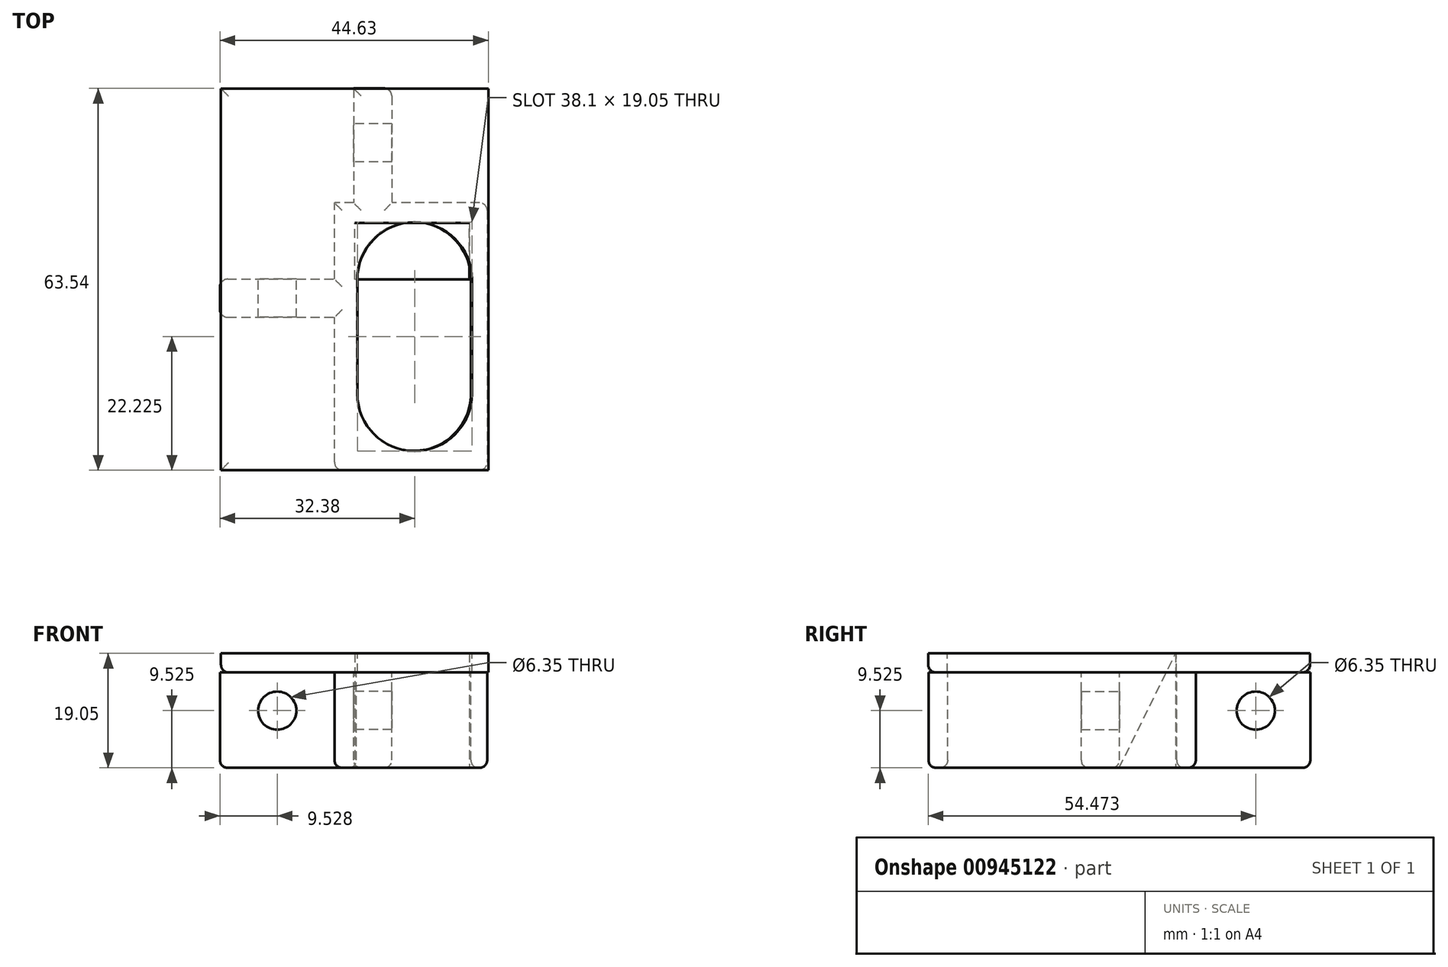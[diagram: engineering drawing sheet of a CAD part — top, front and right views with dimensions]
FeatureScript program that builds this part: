
annotation { "Feature Type Name" : "Feature", "Feature Type Description" : "" }
export const myFeature = defineFeature(function(context is Context, id is Id, definition is map)
    precondition{}
    {
        {
            var Q0;
            Q0=qCreatedBy(makeId("Top.planeOp"),FACE);
            cPlane(context, id + "F0", {"entities" : qUnion([Q0]), "cplaneType" : CPlaneType.OFFSET, "offset" : 3.17 * mm, "oppositeDirection" : true, "width" : 152.4 * mm, "height" : 152.4 * mm});
        }
        {
            var Q0;
            Q0=qCreatedBy(id+"F0.planeOp",FACE);
            var sketch = newSketch(context, id + "F1", { "sketchPlane" : qUnion([Q0])});
            skLineSegment(sketch, "E0.bottom", {"start": v(-22.4, 31.8) * mm, "end": v(22.05, 31.8) * mm});
            skLineSegment(sketch, "E0.top", {"start": v(-22.4, -31.7) * mm, "end": v(22.05, -31.7) * mm});
            skLineSegment(sketch, "E0.left", {"start": v(-22.4, 31.8) * mm, "end": v(-22.4, -31.7) * mm});
            skLineSegment(sketch, "E0.right", {"start": v(22.05, 31.8) * mm, "end": v(22.05, -31.7) * mm});
            skPoint(sketch, "E0.middle", {"position": v(-0.17, 0.04) * mm});
            skLineSegment(sketch, "E1.bottom", {"start": v(22.05, -31.7) * mm, "end": v(-3.35, -31.7) * mm});
            skLineSegment(sketch, "E1.top", {"start": v(22.05, 12.74) * mm, "end": v(-3.35, 12.74) * mm});
            skLineSegment(sketch, "E1.left", {"start": v(22.05, -31.7) * mm, "end": v(22.05, 12.74) * mm});
            skLineSegment(sketch, "E1.right", {"start": v(-3.35, -31.7) * mm, "end": v(-3.35, 12.74) * mm});
            skLineSegment(sketch, "E2", {"start": v(-3.35, 9.57) * mm, "end": v(22.05, 9.57) * mm, "construction": true});
            skLineSegment(sketch, "E3", {"start": v(-3.35, -28.53) * mm, "end": v(22.05, -28.53) * mm, "construction": true});
            skPoint(sketch, "E3.endSnap0", {"position": v(22.05, -9.48) * mm});
            skArc(sketch, "E4", {"start": v(19.33, 0.04) * mm, "mid": v(9.8, 9.57) * mm, "end": v(0.28, 0.04) * mm});
            skLineSegment(sketch, "E5", {"start": v(0.28, 0.04) * mm, "end": v(0.28, -9.48) * mm});
            skLineSegment(sketch, "E6", {"start": v(19.33, 0.04) * mm, "end": v(19.33, -9.48) * mm});
            skLineSegment(sketch, "E7", {"start": v(0.28, -9.48) * mm, "end": v(19.33, -9.48) * mm, "construction": true});
            skLineSegment(sketch, "E8", {"start": v(19.33, -9.48) * mm, "end": v(22.05, -9.48) * mm, "construction": true});
            skArc(sketch, "E9.MirrorCS", {"start": v(19.33, -19) * mm, "mid": v(9.8, -28.53) * mm, "end": v(0.28, -19) * mm});
            skLineSegment(sketch, "E10.MirrorCS", {"start": v(0.28, -19) * mm, "end": v(0.28, -9.48) * mm});
            skLineSegment(sketch, "E11.MirrorCS", {"start": v(19.33, -19) * mm, "end": v(19.33, -9.48) * mm});
            skLineSegment(sketch, "E12", {"start": v(-0.17, 31.8) * mm, "end": v(-0.17, 12.74) * mm});
            skLineSegment(sketch, "E13", {"start": v(6.18, 31.8) * mm, "end": v(6.18, 12.74) * mm});
            skLineSegment(sketch, "E14", {"start": v(-22.4, 0.04) * mm, "end": v(-3.35, 0.04) * mm});
            skLineSegment(sketch, "E15", {"start": v(-22.4, -6.3) * mm, "end": v(-3.35, -6.3) * mm});
            skSolve(sketch);
        }
        {
            var Q0;
            Q0=qCreatedBy(makeId("Top.planeOp"),FACE);
            var sketch = newSketch(context, id + "F2", { "sketchPlane" : qUnion([Q0])});
            skLineSegment(sketch, "E16.bottom", {"start": v(-22.23, 31.75) * mm, "end": v(22.23, 31.75) * mm});
            skLineSegment(sketch, "E16.top", {"start": v(-22.23, -31.75) * mm, "end": v(22.22, -31.75) * mm});
            skLineSegment(sketch, "E16.left", {"start": v(-22.22, 31.75) * mm, "end": v(-22.23, -31.75) * mm});
            skLineSegment(sketch, "E16.right", {"start": v(22.23, 31.75) * mm, "end": v(22.22, -31.75) * mm});
            skPoint(sketch, "E16.middle", {"position": v(0, 0) * mm});
            skLineSegment(sketch, "E17.bottom", {"start": v(22.22, -31.75) * mm, "end": v(-3.18, -31.75) * mm});
            skLineSegment(sketch, "E17.top", {"start": v(22.22, 12.7) * mm, "end": v(-3.18, 12.7) * mm});
            skLineSegment(sketch, "E17.left", {"start": v(22.22, -31.75) * mm, "end": v(22.22, 12.7) * mm});
            skLineSegment(sketch, "E17.right", {"start": v(-3.18, -31.75) * mm, "end": v(-3.18, 12.7) * mm});
            skLineSegment(sketch, "E18", {"start": v(-3.18, 9.53) * mm, "end": v(22.22, 9.53) * mm, "construction": true});
            skLineSegment(sketch, "E19", {"start": v(-3.17, -28.58) * mm, "end": v(22.23, -28.57) * mm, "construction": true});
            skPoint(sketch, "E19.endSnap0", {"position": v(22.23, -9.52) * mm});
            skArc(sketch, "E20", {"start": v(19.5, 0) * mm, "mid": v(9.98, 9.52) * mm, "end": v(0.46, 0) * mm});
            skLineSegment(sketch, "E21", {"start": v(0.46, 0) * mm, "end": v(0.46, -9.53) * mm});
            skLineSegment(sketch, "E22", {"start": v(19.5, 0) * mm, "end": v(19.5, -9.52) * mm});
            skLineSegment(sketch, "E23", {"start": v(0.46, -9.53) * mm, "end": v(19.5, -9.52) * mm, "construction": true});
            skLineSegment(sketch, "E24", {"start": v(19.5, -9.52) * mm, "end": v(22.23, -9.52) * mm, "construction": true});
            skArc(sketch, "E25.MirrorCS", {"start": v(19.5, -19.05) * mm, "mid": v(9.98, -28.57) * mm, "end": v(0.46, -19.05) * mm});
            skLineSegment(sketch, "E26.MirrorCS", {"start": v(0.46, -19.05) * mm, "end": v(0.46, -9.52) * mm});
            skLineSegment(sketch, "E27.MirrorCS", {"start": v(19.5, -19.05) * mm, "end": v(19.5, -9.52) * mm});
            skLineSegment(sketch, "E28", {"start": v(0, 31.75) * mm, "end": v(0, 12.7) * mm});
            skLineSegment(sketch, "E29", {"start": v(6.35, 31.75) * mm, "end": v(6.35, 12.7) * mm});
            skLineSegment(sketch, "E30", {"start": v(-22.23, 0) * mm, "end": v(-3.17, 0) * mm});
            skLineSegment(sketch, "E31", {"start": v(-22.23, -6.35) * mm, "end": v(-3.17, -6.35) * mm});
            skSolve(sketch);
        }
        {
            var Q0;
            {var subQ4=sQuery(id+"F2.wireOp",EDGE,"E28");Q0=makeQuery(id+"F2.imprint","IMPRINT",FACE,{"disambiguationData":[TD([[makeQuery(id+"F2.imprint","IMPRINT",EDGE,{"derivedFrom":subQ4}),-1.0]])]});}
            var Q1;
            {var subQ5=sQuery(id+"F2.wireOp",EDGE,"E31");Q1=makeQuery(id+"F2.imprint","IMPRINT",FACE,{"disambiguationData":[TD([[makeQuery(id+"F2.imprint","IMPRINT",EDGE,{"derivedFrom":subQ5}),-1.0]])]});}
            var Q2;
            {var subQ0=sQuery(id+"F2.wireOp",EDGE,"E29");Q2=makeQuery(id+"F2.imprint","IMPRINT",FACE,{"disambiguationData":[TD([[makeQuery(id+"F2.imprint","IMPRINT",EDGE,{"derivedFrom":subQ0}),1.0]])]});}
            var Q3;
            {var subQ2=sQuery(id+"F2.wireOp",EDGE,"E30");Q3=makeQuery(id+"F2.imprint","IMPRINT",FACE,{"disambiguationData":[TD([[makeQuery(id+"F2.imprint","IMPRINT",EDGE,{"derivedFrom":subQ2}),-1.0]])]});}
            var Q4;
            {var subQ2=sQuery(id+"F2.wireOp",EDGE,"E28");Q4=makeQuery(id+"F2.imprint","IMPRINT",FACE,{"disambiguationData":[TD([[makeQuery(id+"F2.imprint","IMPRINT",EDGE,{"derivedFrom":subQ2}),1.0]])]});}
            var Q5;
            Q5=makeQuery(id+"F2.imprint","IMPRINT",FACE,{"disambiguationData":[TD([[makeQuery(id+"F2.imprint","IMPRINT",EDGE,{"derivedFrom":sQuery(id+"F2.wireOp",EDGE,"E20")}),-1.0]])]});
            extrude(context, id + "F3", {"entities" : qUnion([Q0, Q1, Q2, Q3, Q4, Q5]), "oppositeDirection" : true, "depth" : 3.17 * mm, "offsetDistance" : 25.4 * mm});
        }
        {
            var Q0;
            {var subQ2=sQuery(id+"F1.wireOp",EDGE,"E14");Q0=makeQuery(id+"F1.imprint","IMPRINT",FACE,{"disambiguationData":[TD([[makeQuery(id+"F1.imprint","IMPRINT",EDGE,{"derivedFrom":subQ2}),-1.0]])]});}
            var Q1;
            {var subQ2=sQuery(id+"F1.wireOp",EDGE,"E12");Q1=makeQuery(id+"F1.imprint","IMPRINT",FACE,{"disambiguationData":[TD([[makeQuery(id+"F1.imprint","IMPRINT",EDGE,{"derivedFrom":subQ2}),1.0]])]});}
            var Q2;
            Q2=makeQuery(id+"F1.imprint","IMPRINT",FACE,{"disambiguationData":[TD([[makeQuery(id+"F1.imprint","IMPRINT",EDGE,{"derivedFrom":sQuery(id+"F1.wireOp",EDGE,"E4")}),-1.0]])]});
            extrude(context, id + "F4", {"entities" : qUnion([Q0, Q1, Q2]), "oppositeDirection" : true, "depth" : 15.88 * mm, "offsetDistance" : 25.4 * mm});
        }
        {
            var Q0;
            Q0=qCreatedBy(makeId("Front.planeOp"),FACE);
            var sketch = newSketch(context, id + "F5", { "sketchPlane" : qUnion([Q0])});
            skCircle(sketch, "E32", {"center": v(-12.87, -9.53) * mm, "radius": 3.18 * mm});
            skSolve(sketch);
        }
        {
            var Q0;
            Q0=makeQuery(id+"F5.imprint","IMPRINT",FACE,{"disambiguationData":[TD([[makeQuery(id+"F5.imprint","IMPRINT",EDGE,{"derivedFrom":sQuery(id+"F5.wireOp",EDGE,"E32")}),1.0]])]});
            extrude(context, id + "F6", {"entities" : qUnion([Q0]), "operationType" : NewBodyOperationType.REMOVE, "endBound" : BoundingType.SYMMETRIC, "depth" : 25.4 * mm, "offsetDistance" : 25.4 * mm});
        }
        {
            var Q0;
            Q0=qCreatedBy(makeId("Right.planeOp"),FACE);
            var sketch = newSketch(context, id + "F7", { "sketchPlane" : qUnion([Q0])});
            skCircle(sketch, "E33", {"center": v(22.72, -9.53) * mm, "radius": 3.18 * mm});
            skLineSegment(sketch, "E34", {"start": v(9.42, 0) * mm, "end": v(9.42, -19.05) * mm});
            skLineSegment(sketch, "E35", {"start": v(9.42, -19.05) * mm, "end": v(0, -19.05) * mm});
            skLineSegment(sketch, "E36", {"start": v(0, -19.05) * mm, "end": v(9.42, 0) * mm});
            skLineSegment(sketch, "E37", {"start": v(0, -3.18) * mm, "end": v(-6.35, -3.18) * mm, "construction": true});
            skSolve(sketch);
        }
        {
            var Q0;
            Q0=makeQuery(id+"F7.imprint","IMPRINT",FACE,{"disambiguationData":[TD([[makeQuery(id+"F7.imprint","IMPRINT",EDGE,{"derivedFrom":sQuery(id+"F7.wireOp",EDGE,"E33")}),1.0]])]});
            extrude(context, id + "F8", {"entities" : qUnion([Q0]), "operationType" : NewBodyOperationType.REMOVE, "endBound" : BoundingType.SYMMETRIC, "depth" : 25.4 * mm, "offsetDistance" : 25.4 * mm});
        }
        {
            var Q0;
            Q0=makeQuery(id+"F7.imprint","IMPRINT",FACE,{"disambiguationData":[TD([[makeQuery(id+"F7.imprint","IMPRINT",EDGE,{"derivedFrom":sQuery(id+"F7.wireOp",EDGE,"E34")}),-1.0]])]});
            extrude(context, id + "F9", {"entities" : qUnion([Q0]), "depth" : 19.05 * mm, "offsetDistance" : 25.4 * mm});
        }
        {
            var Q0;
            Q0=makeQuery(id+"F4.opExtrude","SWEPT_EDGE",EDGE,{"disambiguationData":[OSD([sQuery(id+"F1.wireOp",EDGE,"E0.left"),sQuery(id+"F1.wireOp",EDGE,"E15")])]});
            var Q1;
            Q1=makeQuery(id+"F4.opExtrude","SWEPT_EDGE",EDGE,{"disambiguationData":[OSD([sQuery(id+"F1.wireOp",EDGE,"E0.left"),sQuery(id+"F1.wireOp",EDGE,"E14")])]});
            var Q2;
            Q2=makeQuery(id+"F4.opExtrude","CAP_EDGE",EDGE,{"disambiguationData":[OSD([sQuery(id+"F1.wireOp",EDGE,"E14")])],"isStart":false});
            var Q3;
            Q3=makeQuery(id+"F4.opExtrude","CAP_EDGE",EDGE,{"disambiguationData":[OSD([sQuery(id+"F1.wireOp",EDGE,"E0.left")])],"isStart":false});
            var Q4;
            Q4=makeQuery(id+"F4.opExtrude","CAP_FACE",FACE,{"disambiguationData":[OSD([sQuery(id+"F1.wireOp",EDGE,"E0.bottom"),sQuery(id+"F1.wireOp",EDGE,"E0.top"),sQuery(id+"F1.wireOp",EDGE,"E0.left"),sQuery(id+"F1.wireOp",EDGE,"E0.right"),sQuery(id+"F1.wireOp",EDGE,"E1.top"),sQuery(id+"F1.wireOp",EDGE,"E1.right"),sQuery(id+"F1.wireOp",EDGE,"E4"),sQuery(id+"F1.wireOp",EDGE,"E5"),sQuery(id+"F1.wireOp",EDGE,"E6"),sQuery(id+"F1.wireOp",EDGE,"E9.MirrorCS"),sQuery(id+"F1.wireOp",EDGE,"E10.MirrorCS"),sQuery(id+"F1.wireOp",EDGE,"E11.MirrorCS"),sQuery(id+"F1.wireOp",EDGE,"E12"),sQuery(id+"F1.wireOp",EDGE,"E13"),sQuery(id+"F1.wireOp",EDGE,"E14"),sQuery(id+"F1.wireOp",EDGE,"E15")])],"isStart":false});
            var Q5;
            Q5=makeQuery(id+"F3.opExtrude","CAP_EDGE",EDGE,{"disambiguationData":[OSD([sQuery(id+"F2.wireOp",EDGE,"E16.left")])],"isStart":false});
            var Q6;
            Q6=makeQuery(id+"F3.opExtrude","CAP_EDGE",EDGE,{"disambiguationData":[OSD([sQuery(id+"F2.wireOp",EDGE,"E16.top")])],"isStart":false});
            var Q7;
            Q7=makeQuery(id+"F4.opExtrude","SWEPT_EDGE",EDGE,{"disambiguationData":[OSD([sQuery(id+"F1.wireOp",EDGE,"E0.top"),sQuery(id+"F1.wireOp",EDGE,"E1.right")])]});
            var Q8;
            Q8=makeQuery(id+"F4.opExtrude","SWEPT_EDGE",EDGE,{"disambiguationData":[OSD([sQuery(id+"F1.wireOp",EDGE,"E0.top"),sQuery(id+"F1.wireOp",EDGE,"E0.right")])]});
            var Q9;
            Q9=makeQuery(id+"F4.opExtrude","SWEPT_EDGE",EDGE,{"disambiguationData":[OSD([sQuery(id+"F1.wireOp",EDGE,"E0.right"),sQuery(id+"F1.wireOp",EDGE,"E1.top")])]});
            var Q10;
            Q10=makeQuery(id+"F4.opExtrude","SWEPT_EDGE",EDGE,{"disambiguationData":[OSD([sQuery(id+"F1.wireOp",EDGE,"E0.bottom"),sQuery(id+"F1.wireOp",EDGE,"E13")])]});
            var Q11;
            Q11=makeQuery(id+"F3.opExtrude","CAP_EDGE",EDGE,{"disambiguationData":[OSD([sQuery(id+"F2.wireOp",EDGE,"E16.bottom")])],"isStart":false});
            fillet(context, id + "F10", {"entities" : qUnion([Q0, Q1, Q2, Q3, Q4, Q5, Q6, Q7, Q8, Q9, Q10, Q11]), "radius" : 1.27 * mm, "tangentPropagation" : true, "allowEdgeOverflow" : false});
        }
    });
